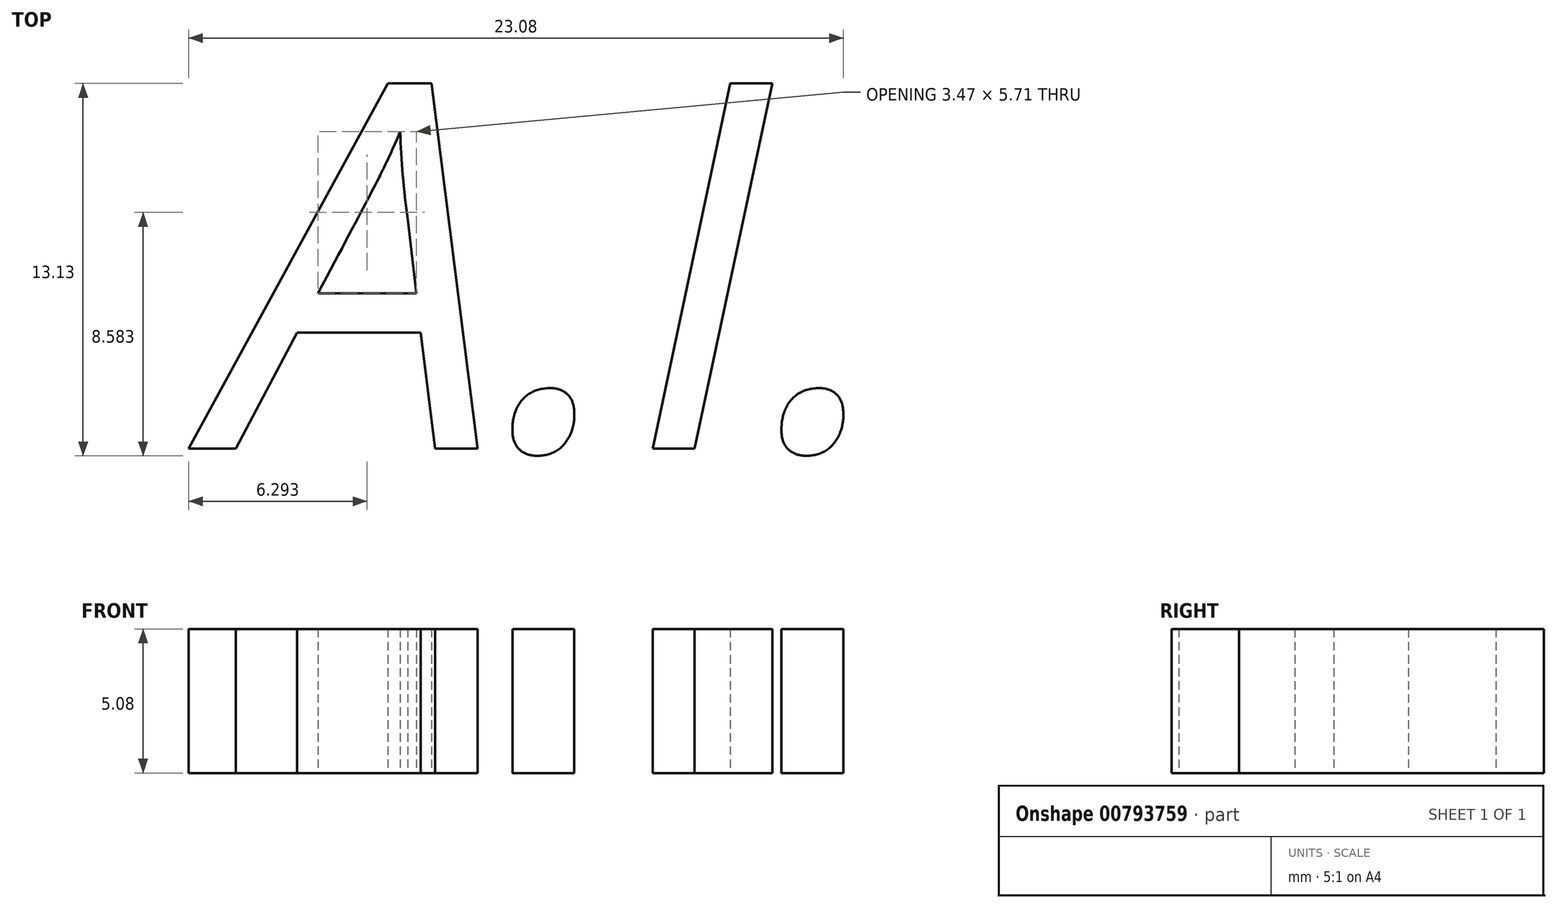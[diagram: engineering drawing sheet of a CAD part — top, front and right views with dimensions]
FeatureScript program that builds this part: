
annotation { "Feature Type Name" : "Feature", "Feature Type Description" : "" }
export const myFeature = defineFeature(function(context is Context, id is Id, definition is map)
    precondition{}
    {
        {
            var Q0;
            Q0=qCreatedBy(makeId("Top.planeOp"),FACE);
            var sketch = newSketch(context, id + "F0", { "sketchPlane" : qUnion([Q0])});
            skText(sketch, "E0", { "text": "A.I.", "fontName": "OpenSans-Italic.ttf"});
            const initialGuessF0  = {"E0": [-0.02425, 0, 1, 0, 0.01298]};
            skSetInitialGuess(sketch, initialGuessF0);
            skSolve(sketch);
        }
        {
            var Q0;
            Q0 = qSketchRegion(id + "F0", true);
            extrude(context, id + "F1", {"entities" : qUnion([Q0]), "depth" : 5.08 * mm, "offsetDistance" : 25.4 * mm});
        }
    });
